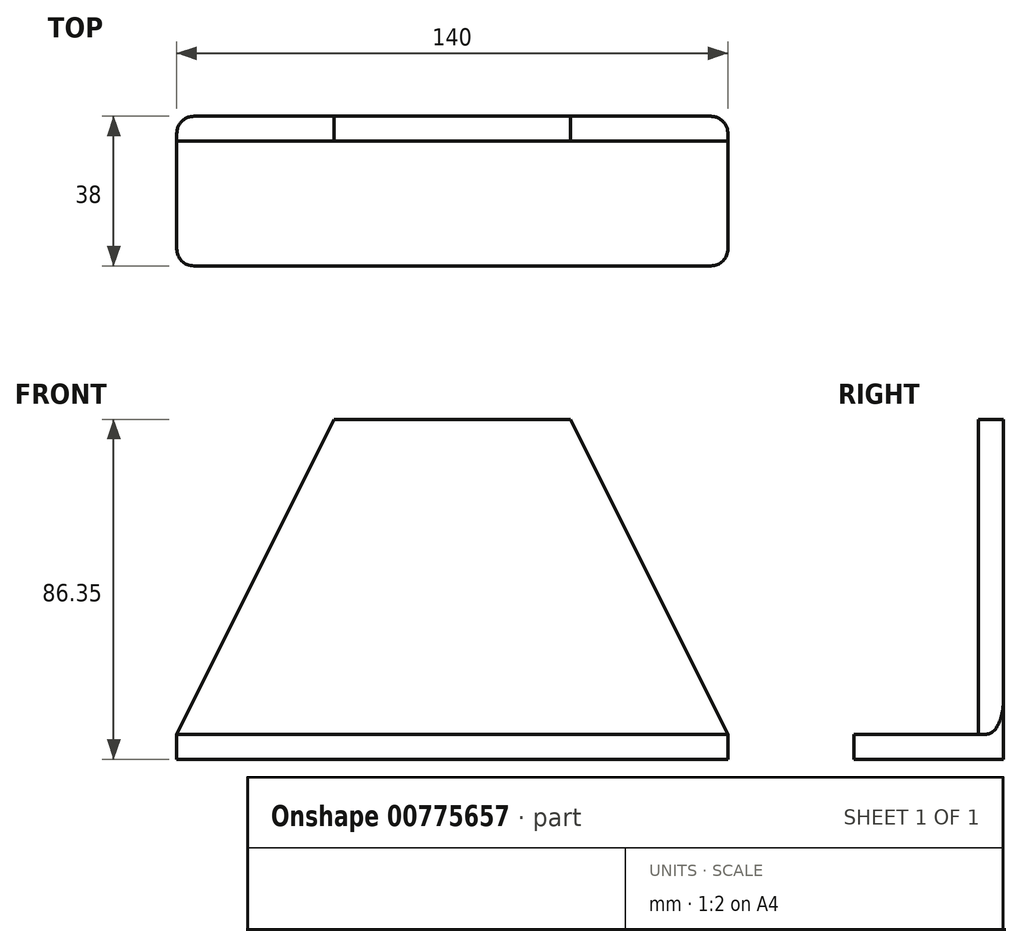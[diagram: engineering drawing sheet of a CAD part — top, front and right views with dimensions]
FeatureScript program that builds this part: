
annotation { "Feature Type Name" : "Feature", "Feature Type Description" : "" }
export const myFeature = defineFeature(function(context is Context, id is Id, definition is map)
    precondition{}
    {
        {
            var Q0;
            Q0=qCreatedBy(makeId("Top.planeOp"),FACE);
            var sketch = newSketch(context, id + "F0", { "sketchPlane" : qUnion([Q0])});
            skLineSegment(sketch, "E0.bottom", {"start": v(70, -15.82) * mm, "end": v(-70, -15.83) * mm});
            skLineSegment(sketch, "E0.top", {"start": v(70, 15.83) * mm, "end": v(-70, 15.82) * mm});
            skLineSegment(sketch, "E0.left", {"start": v(70, -15.82) * mm, "end": v(70, 15.83) * mm});
            skLineSegment(sketch, "E0.right", {"start": v(-70, -15.83) * mm, "end": v(-70, 15.82) * mm});
            skPoint(sketch, "E0.middle", {"position": v(0, 0) * mm});
            skSolve(sketch);
        }
        {
            var Q0;
            Q0=makeQuery(id+"F0.imprint","IMPRINT",FACE,{"disambiguationData":[TD([[makeQuery(id+"F0.imprint","IMPRINT",EDGE,{"derivedFrom":sQuery(id+"F0.wireOp",EDGE,"E0.bottom")}),-1.0]])]});
            extrude(context, id + "F1", {"entities" : qUnion([Q0]), "depth" : 6.35 * mm, "offsetDistance" : 25 * mm});
        }
        {
            var Q0;
            Q0=makeQuery(id+"F1.opExtrude","SWEPT_FACE",FACE,{"disambiguationData":[OSD([sQuery(id+"F0.wireOp",EDGE,"E0.top")])]});
            var sketch = newSketch(context, id + "F2", { "sketchPlane" : qUnion([Q0])});
            skLineSegment(sketch, "E1", {"start": v(-70, 6.35) * mm, "end": v(-30, 86.35) * mm});
            skLineSegment(sketch, "E2", {"start": v(-30, 86.35) * mm, "end": v(30, 86.35) * mm});
            skLineSegment(sketch, "E3", {"start": v(30, 86.35) * mm, "end": v(70, 6.35) * mm});
            skSolve(sketch);
        }
        {
            var Q0;
            {var subQ0=sQuery(id+"F0.wireOp",EDGE,"E0.top");Q0=makeQuery(id+"F2.imprint","IMPRINT",FACE,{"disambiguationData":[TD([[makeQuery(id+"F2.imprint","IMPRINT",EDGE,{"derivedFrom":makeQuery(id+"F1.opExtrude","CAP_EDGE",EDGE,{"disambiguationData":[OSD([subQ0])],"isStart":true})}),1.0]])]});}
            var Q1;
            Q1=makeQuery(id+"F2.imprint","IMPRINT",FACE,{"disambiguationData":[TD([[makeQuery(id+"F2.imprint","IMPRINT",EDGE,{"derivedFrom":sQuery(id+"F2.wireOp",EDGE,"E1")}),-1.0]])]});
            extrude(context, id + "F3", {"entities" : qUnion([Q0, Q1]), "operationType" : NewBodyOperationType.ADD, "depth" : 6.35 * mm, "offsetDistance" : 25 * mm});
        }
        {
            var Q0;
            Q0=makeQuery(id+"F1.opExtrude","SWEPT_EDGE",EDGE,{"disambiguationData":[OSD([sQuery(id+"F0.wireOp",EDGE,"E0.bottom"),sQuery(id+"F0.wireOp",EDGE,"E0.right")])]});
            var Q1;
            Q1=makeQuery(id+"F3.opExtrude","CAP_EDGE",EDGE,{"disambiguationData":[OSD([sQuery(id+"F0.wireOp",EDGE,"E0.top"),sQuery(id+"F0.wireOp",EDGE,"E0.right")])],"isStart":false});
            var Q2;
            Q2=makeQuery(id+"F1.opExtrude","SWEPT_EDGE",EDGE,{"disambiguationData":[OSD([sQuery(id+"F0.wireOp",EDGE,"E0.bottom"),sQuery(id+"F0.wireOp",EDGE,"E0.left")])]});
            var Q3;
            Q3=makeQuery(id+"F3.opExtrude","CAP_EDGE",EDGE,{"disambiguationData":[OSD([sQuery(id+"F0.wireOp",EDGE,"E0.top"),sQuery(id+"F0.wireOp",EDGE,"E0.left")])],"isStart":false});
            fillet(context, id + "F4", {"entities" : qUnion([Q0, Q1, Q2, Q3]), "radius" : 4.33 * mm, "tangentPropagation" : true, "allowEdgeOverflow" : false});
        }
    });
